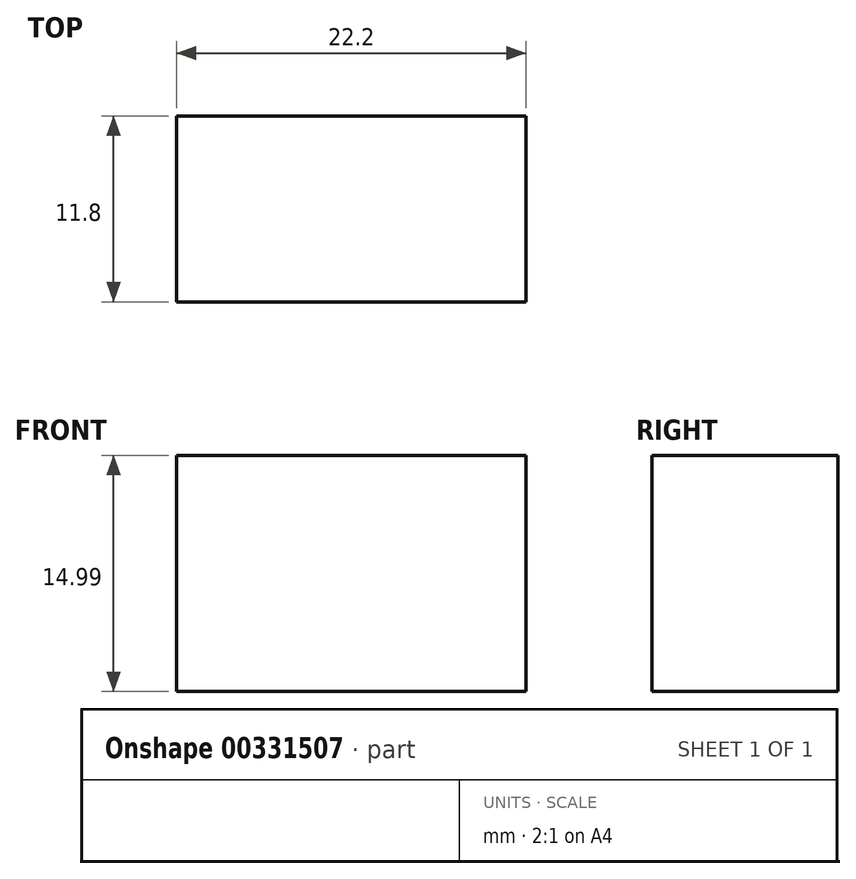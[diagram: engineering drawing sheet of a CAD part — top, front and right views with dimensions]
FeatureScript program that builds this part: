
annotation { "Feature Type Name" : "Feature", "Feature Type Description" : "" }
export const myFeature = defineFeature(function(context is Context, id is Id, definition is map)
    precondition{}
    {
        {
            var Q0;
            Q0=qCreatedBy(makeId("Top.planeOp"),FACE);
            var sketch = newSketch(context, id + "F0", { "sketchPlane" : qUnion([Q0])});
            skLineSegment(sketch, "E0.bottom", {"start": v(11.1, 5.9) * mm, "end": v(-11.1, 5.9) * mm});
            skLineSegment(sketch, "E0.top", {"start": v(11.1, -5.9) * mm, "end": v(-11.1, -5.9) * mm});
            skLineSegment(sketch, "E0.left", {"start": v(11.1, 5.9) * mm, "end": v(11.1, -5.9) * mm});
            skLineSegment(sketch, "E0.right", {"start": v(-11.1, 5.9) * mm, "end": v(-11.1, -5.9) * mm});
            skPoint(sketch, "E0.middle", {"position": v(0, 0) * mm});
            skSolve(sketch);
        }
        {
            var Q0;
            Q0=makeQuery(id+"F0.imprint","IMPRINT",FACE,{"disambiguationData":[TD([[makeQuery(id+"F0.imprint","IMPRINT",EDGE,{"derivedFrom":sQuery(id+"F0.wireOp",EDGE,"E0.bottom")}),1.0]])]});
            extrude(context, id + "F1", {"entities" : qUnion([Q0]), "depth" : 15 * mm});
        }
    });
